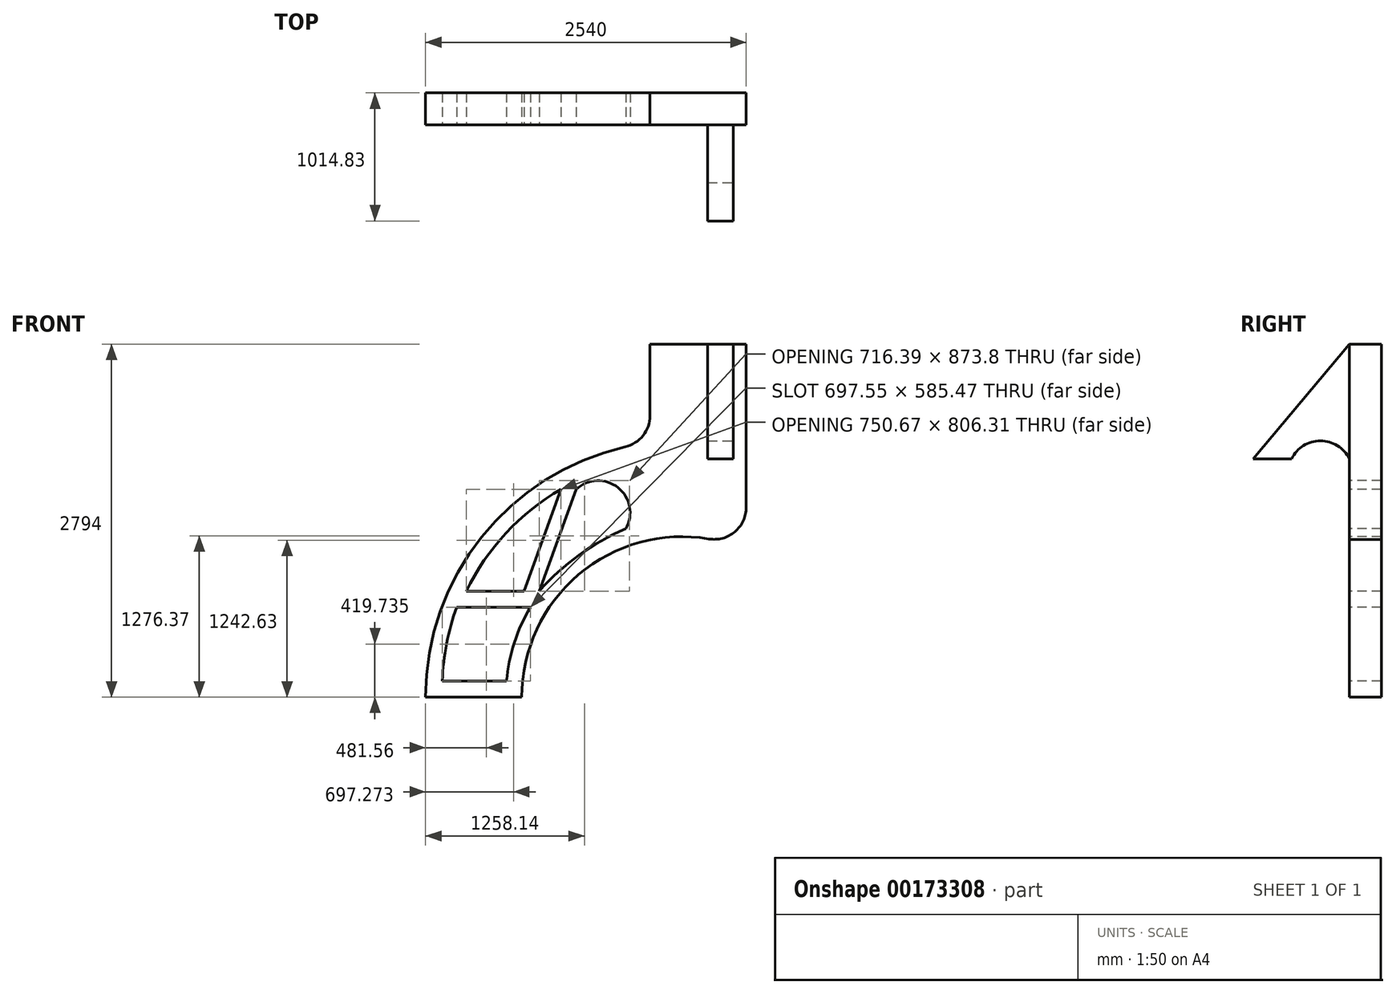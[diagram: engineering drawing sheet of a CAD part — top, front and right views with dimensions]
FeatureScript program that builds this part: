
annotation { "Feature Type Name" : "Feature", "Feature Type Description" : "" }
export const myFeature = defineFeature(function(context is Context, id is Id, definition is map)
    precondition{}
    {
        {
            var Q0;
            Q0=qCreatedBy(makeId("Front.planeOp"),FACE);
            var sketch = newSketch(context, id + "F0", { "sketchPlane" : qUnion([Q0])});
            skArc(sketch, "E0", {"start": v(1103.46, 412.77) * mm, "mid": v(72, 130.5) * mm, "end": v(-378.21, -839.47) * mm});
            skArc(sketch, "E1.0", {"start": v(440.23, 1141.72) * mm, "mid": v(-696.7, 427.7) * mm, "end": v(-1140.21, -839.47) * mm});
            skLineSegment(sketch, "E2", {"start": v(-378.21, -839.47) * mm, "end": v(-1140.21, -839.47) * mm});
            skLineSegment(sketch, "E3", {"start": v(1399.79, 1954.53) * mm, "end": v(637.79, 1954.53) * mm});
            skLineSegment(sketch, "E4", {"start": v(637.79, 1954.53) * mm, "end": v(637.79, 1389.37) * mm});
            skLineSegment(sketch, "E5", {"start": v(1399.79, 663.21) * mm, "end": v(1399.79, 1954.53) * mm});
            skPoint(sketch, "E6.visualSharp", {"position": v(1399.79, 324.5) * mm});
            skArc(sketch, "E6.filletArc", {"start": v(1103.46, 412.77) * mm, "mid": v(1309.75, 469.22) * mm, "end": v(1399.79, 663.21) * mm});
            skPoint(sketch, "E7.visualSharp", {"position": v(637.79, 1176.6) * mm});
            skArc(sketch, "E7.filletArc", {"start": v(440.23, 1141.72) * mm, "mid": v(582.35, 1230.97) * mm, "end": v(637.79, 1389.37) * mm});
            skLineSegment(sketch, "E8", {"start": v(-1007.43, -712.47) * mm, "end": v(-499.43, -712.47) * mm});
            skLineSegment(sketch, "E9", {"start": v(-894.07, -127) * mm, "end": v(-309.87, -127) * mm});
            skLineSegment(sketch, "E10", {"start": v(-818.27, 0) * mm, "end": v(-361.07, 0) * mm});
            skLineSegment(sketch, "E11", {"start": v(-361.07, 0) * mm, "end": v(-67.6, 806.31) * mm});
            skLineSegment(sketch, "E12", {"start": v(1399.79, 1954.53) * mm, "end": v(1298.19, 1954.53) * mm});
            skLineSegment(sketch, "E13", {"start": v(1399.79, 1954.53) * mm, "end": v(1018.79, 1954.53) * mm});
            skLineSegment(sketch, "E14", {"start": v(1399.79, 1954.53) * mm, "end": v(1094.99, 1954.53) * mm});
            skLineSegment(sketch, "E15", {"start": v(1298.19, 1954.53) * mm, "end": v(1298.19, 1192.53) * mm});
            skLineSegment(sketch, "E16", {"start": v(1094.99, 1954.53) * mm, "end": v(1094.99, 1192.53) * mm});
            skLineSegment(sketch, "E17", {"start": v(1094.99, 1192.53) * mm, "end": v(1298.19, 1192.53) * mm});
            skArc(sketch, "E18", {"start": v(-67.6, 806.31) * mm, "mid": v(-502.5, 458.6) * mm, "end": v(-818.27, 0) * mm});
            skArc(sketch, "E19", {"start": v(-894.07, -127) * mm, "mid": v(-973.8, -415.27) * mm, "end": v(-1007.43, -712.47) * mm});
            skArc(sketch, "E20", {"start": v(-309.87, -127) * mm, "mid": v(-437.29, -409.17) * mm, "end": v(-499.43, -712.47) * mm});
            skLineSegment(sketch, "E21", {"start": v(53.21, 806.31) * mm, "end": v(-240.26, 0) * mm});
            skArc(sketch, "E22", {"start": v(445.46, 492.4) * mm, "mid": v(74.98, 284.67) * mm, "end": v(-240.26, 0) * mm});
            skArc(sketch, "E23", {"start": v(445.46, 492.4) * mm, "mid": v(384.52, 818.28) * mm, "end": v(53.21, 806.31) * mm});
            skSolve(sketch);
        }
        {
            var Q0;
            Q0=makeQuery(id+"F0.imprint","IMPRINT",FACE,{"disambiguationData":[TD([[makeQuery(id+"F0.imprint","IMPRINT",EDGE,{"derivedFrom":sQuery(id+"F0.wireOp",EDGE,"E0")}),-1.0]])]});
            extrude(context, id + "F1", {"entities" : qUnion([Q0]), "oppositeDirection" : true, "depth" : 254 * mm});
        }
        {
            var Q0;
            {var subQ2=sQuery(id+"F0.wireOp",EDGE,"E15");Q0=makeQuery(id+"F0.imprint","IMPRINT",FACE,{"disambiguationData":[TD([[makeQuery(id+"F0.imprint","IMPRINT",EDGE,{"derivedFrom":subQ2}),-1.0]])]});}
            extrude(context, id + "F2", {"entities" : qUnion([Q0]), "operationType" : NewBodyOperationType.ADD, "oppositeDirection" : true, "depth" : 254 * mm});
        }
        {
            var Q0;
            Q0=makeQuery(id+"F1.opExtrude","SWEPT_FACE",FACE,{"disambiguationData":[OSD([sQuery(id+"F0.wireOp",EDGE,"E5")])]});
            var sketch = newSketch(context, id + "F3", { "sketchPlane" : qUnion([Q0])});
            skLineSegment(sketch, "E24", {"start": v(0, 1954.53) * mm, "end": v(-760.83, 1047.8) * mm});
            skLineSegment(sketch, "E25", {"start": v(-760.83, 1047.8) * mm, "end": v(-456.03, 1047.8) * mm});
            skArc(sketch, "E26", {"start": v(0, 1047.8) * mm, "mid": v(-228.01, 1189.9) * mm, "end": v(-456.03, 1047.8) * mm});
            skSolve(sketch);
        }
        {
            var Q0;
            {var subQ0=sQuery(id+"F3.wireOp",EDGE,"E24");Q0=makeQuery(id+"F3.imprint","IMPRINT",FACE,{"disambiguationData":[TD([[makeQuery(id+"F3.imprint","IMPRINT",EDGE,{"derivedFrom":subQ0}),1.0]])]});}
            extrude(context, id + "F4", {"entities" : qUnion([Q0]), "operationType" : NewBodyOperationType.ADD, "oppositeDirection" : true, "depth" : 304.8 * mm, "hasSecondDirection" : true, "secondDirectionOppositeDirection" : true, "secondDirectionDepth" : 101.6 * mm});
        }
    });
